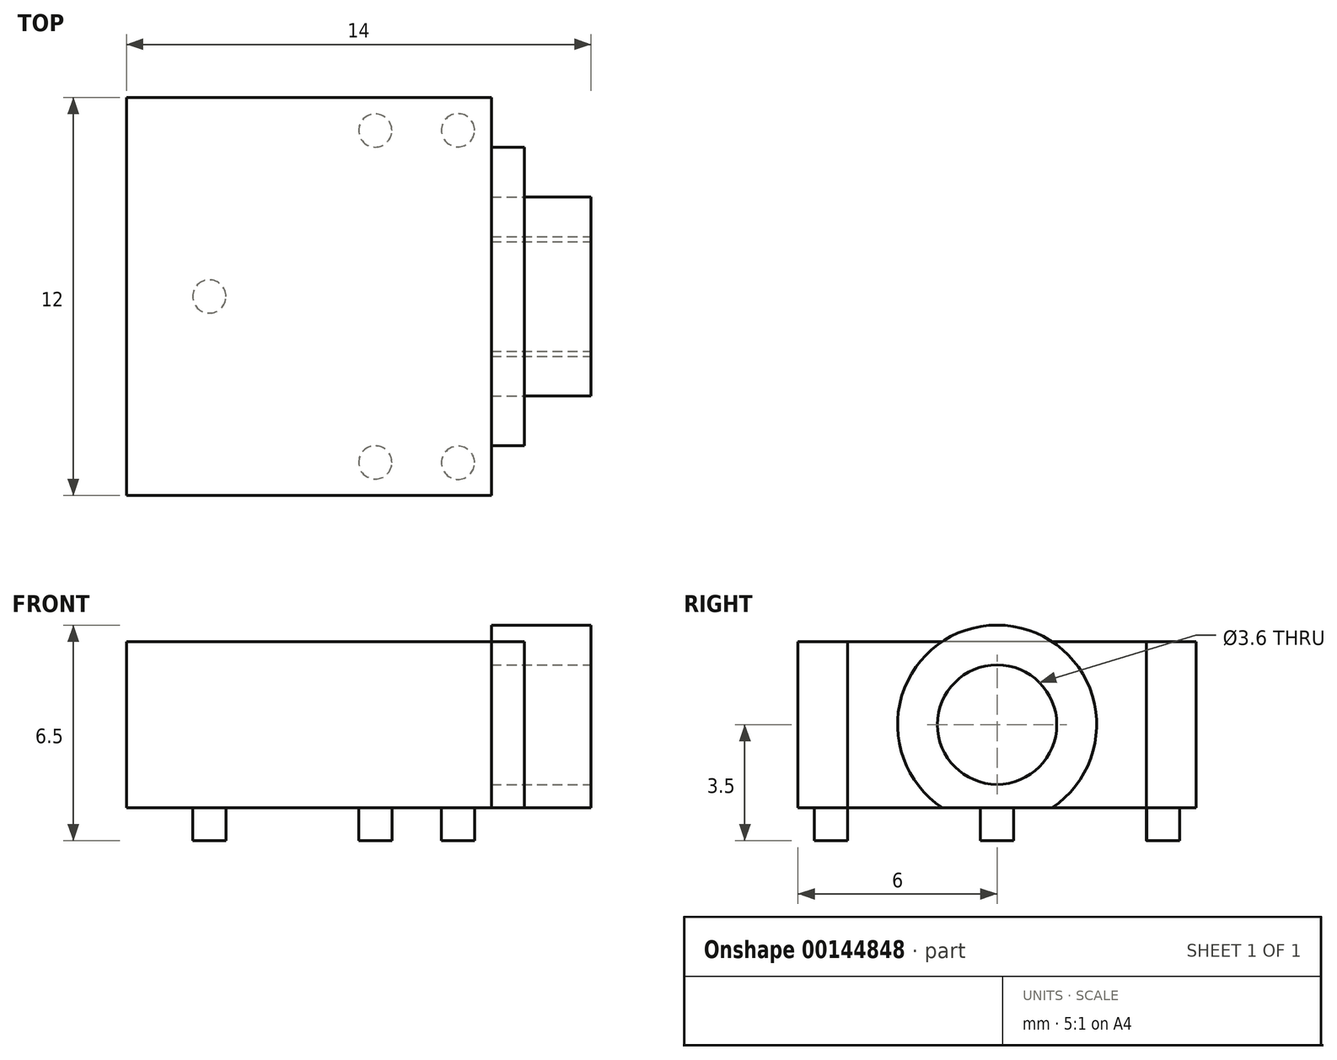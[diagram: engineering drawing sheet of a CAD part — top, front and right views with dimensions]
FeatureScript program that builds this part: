
annotation { "Feature Type Name" : "Feature", "Feature Type Description" : "" }
export const myFeature = defineFeature(function(context is Context, id is Id, definition is map)
    precondition{}
    {
        {
            var Q0;
            Q0=qCreatedBy(makeId("Right.planeOp"),FACE);
            var sketch = newSketch(context, id + "F0", { "sketchPlane" : qUnion([Q0])});
            skCircle(sketch, "E0", {"center": v(0, 0) * mm, "radius": 1.8 * mm});
            skCircle(sketch, "E1", {"center": v(0, 0) * mm, "radius": 3 * mm});
            skLineSegment(sketch, "E2.top", {"start": v(-1.65, -2.5) * mm, "end": v(4.5, -2.5) * mm});
            skLineSegment(sketch, "E3.top", {"start": v(4.5, -2.5) * mm, "end": v(6.02, -2.5) * mm});
            skSolve(sketch);
        }
        {
            var Q0;
            Q0=makeQuery(id+"F0.imprint","IMPRINT",FACE,{"disambiguationData":[TD([[makeQuery(id+"F0.imprint","IMPRINT",EDGE,{"derivedFrom":sQuery(id+"F0.wireOp",EDGE,"E0")}),-1.0]])]});
            var Q1;
            {var subQ0=sQuery(id+"F0.wireOp",EDGE,"E3.top");var subQ1=sQuery(id+"F0.wireOp",EDGE,"E1");var subQ2=makeQuery(id+"F0.imprint","INTERSECT",VERTEX,{"disambiguationData":[OD(0.0)],"derivedFrom":[subQ1,subQ0]});Q1=makeQuery(id+"F0.imprint","IMPRINT",FACE,{"disambiguationData":[TD([[makeQuery(id+"F0.imprint","IMPRINT",EDGE,{"disambiguationData":[TD([[subQ2,-1.0]])],"derivedFrom":subQ1}),1.0]])]});}
            var Q2;
            {var subQ0=sQuery(id+"F0.wireOp",EDGE,"E3.bottom");var subQ1=sQuery(id+"F0.wireOp",EDGE,"E1");var subQ2=makeQuery(id+"F0.imprint","INTERSECT",VERTEX,{"disambiguationData":[OD(0.0)],"derivedFrom":[subQ1,subQ0]});Q2=makeQuery(id+"F0.imprint","IMPRINT",FACE,{"disambiguationData":[TD([[makeQuery(id+"F0.imprint","IMPRINT",EDGE,{"disambiguationData":[TD([[subQ2,-1.0]])],"derivedFrom":subQ1}),1.0]])]});}
            extrude(context, id + "F1", {"entities" : qUnion([Q0, Q1, Q2]), "oppositeDirection" : true, "depth" : 3 * mm});
        }
        {
            var Q0;
            Q0=makeQuery(id+"F1.opExtrude","CAP_FACE",FACE,{"disambiguationData":[OSD([sQuery(id+"F0.wireOp",EDGE,"E0"),sQuery(id+"F0.wireOp",EDGE,"E1")])],"isStart":false});
            var sketch = newSketch(context, id + "F2", { "sketchPlane" : qUnion([Q0])});
            skLineSegment(sketch, "E4.bottom", {"start": v(-4.5, 2.5) * mm, "end": v(4.5, 2.5) * mm});
            skLineSegment(sketch, "E4.top", {"start": v(-4.5, -2.5) * mm, "end": v(4.5, -2.5) * mm});
            skLineSegment(sketch, "E4.left", {"start": v(-4.5, 2.5) * mm, "end": v(-4.5, -2.5) * mm});
            skLineSegment(sketch, "E4.right", {"start": v(4.5, 2.5) * mm, "end": v(4.5, -2.5) * mm});
            skSolve(sketch);
        }
        {
            var Q0;
            Q0 = qSketchRegion(id + "F2", true);
            extrude(context, id + "F3", {"entities" : qUnion([Q0]), "oppositeDirection" : true, "depth" : 1 * mm});
        }
        {
            var Q0;
            Q0=makeQuery(id+"F3.boolean.opBoolean","MERGE",FACE,{"derivedFrom":[makeQuery(id+"F1.opExtrude","CAP_FACE",FACE,{"disambiguationData":[OSD([sQuery(id+"F0.wireOp",EDGE,"E0"),sQuery(id+"F0.wireOp",EDGE,"E1")])],"isStart":false}),makeQuery(id+"F3.opExtrude","CAP_FACE",FACE,{"disambiguationData":[OSD([sQuery(id+"F2.wireOp",EDGE,"E4.bottom"),sQuery(id+"F2.wireOp",EDGE,"E4.top"),sQuery(id+"F2.wireOp",EDGE,"E4.left"),sQuery(id+"F2.wireOp",EDGE,"E4.right")])],"isStart":true})]});
            var sketch = newSketch(context, id + "F4", { "sketchPlane" : qUnion([Q0])});
            skLineSegment(sketch, "E5.bottom", {"start": v(-6, 2.5) * mm, "end": v(6, 2.5) * mm});
            skLineSegment(sketch, "E5.top", {"start": v(-6, -2.5) * mm, "end": v(6, -2.5) * mm});
            skLineSegment(sketch, "E5.left", {"start": v(-6, 2.5) * mm, "end": v(-6, -2.5) * mm});
            skLineSegment(sketch, "E5.right", {"start": v(6, 2.5) * mm, "end": v(6, -2.5) * mm});
            skSolve(sketch);
        }
        {
            var Q0;
            Q0 = qSketchRegion(id + "F4", true);
            extrude(context, id + "F5", {"entities" : qUnion([Q0]), "depth" : 11 * mm});
        }
        {
            var Q0;
            Q0=makeQuery(id+"F5.boolean.opBoolean","MERGE",FACE,{"derivedFrom":[dummyQuery(id+"FQrOcedIkoS32uB.importOp",FACE,7.0),makeQuery(id+"F5.opExtrude","SWEPT_FACE",FACE,{"disambiguationData":[OSD([sQuery(id+"F4.wireOp",EDGE,"E5.top")])]})]});
            var sketch = newSketch(context, id + "F6", { "sketchPlane" : qUnion([Q0])});
            skCircle(sketch, "E6", {"center": v(-6.5, 5) * mm, "radius": 0.5 * mm});
            skCircle(sketch, "E7", {"center": v(-4, -5) * mm, "radius": 0.5 * mm});
            skCircle(sketch, "E8", {"center": v(-6.5, -5) * mm, "radius": 0.5 * mm});
            skCircle(sketch, "E9", {"center": v(-11.5, 0) * mm, "radius": 0.5 * mm});
            skCircle(sketch, "E10", {"center": v(-4, 5) * mm, "radius": 0.5 * mm});
            skLineSegment(sketch, "E11", {"start": v(0, 0) * mm, "end": v(-14.57, 0) * mm, "construction": true});
            skSolve(sketch);
        }
        {
            var Q0;
            Q0=makeQuery(id+"F6.imprint","IMPRINT",FACE,{"disambiguationData":[TD([[makeQuery(id+"F6.imprint","IMPRINT",EDGE,{"derivedFrom":sQuery(id+"F6.wireOp",EDGE,"E10")}),1.0]])]});
            var Q1;
            Q1=makeQuery(id+"F6.imprint","IMPRINT",FACE,{"disambiguationData":[TD([[makeQuery(id+"F6.imprint","IMPRINT",EDGE,{"derivedFrom":sQuery(id+"F6.wireOp",EDGE,"E9")}),1.0]])]});
            var Q2;
            Q2=makeQuery(id+"F6.imprint","IMPRINT",FACE,{"disambiguationData":[TD([[makeQuery(id+"F6.imprint","IMPRINT",EDGE,{"derivedFrom":sQuery(id+"F6.wireOp",EDGE,"E8")}),1.0]])]});
            var Q3;
            Q3=makeQuery(id+"F6.imprint","IMPRINT",FACE,{"disambiguationData":[TD([[makeQuery(id+"F6.imprint","IMPRINT",EDGE,{"derivedFrom":sQuery(id+"F6.wireOp",EDGE,"E6")}),1.0]])]});
            var Q4;
            Q4=makeQuery(id+"F6.imprint","IMPRINT",FACE,{"disambiguationData":[TD([[makeQuery(id+"F6.imprint","IMPRINT",EDGE,{"derivedFrom":sQuery(id+"F6.wireOp",EDGE,"E7")}),1.0]])]});
            var Q5;
            Q5=sQuery(id+"F6.wireOp",EDGE,"E10");
            var Q6;
            Q6=sQuery(id+"F6.wireOp",EDGE,"E6");
            var Q7;
            Q7=sQuery(id+"F6.wireOp",EDGE,"E9");
            var Q8;
            Q8=sQuery(id+"F6.wireOp",EDGE,"E8");
            var Q9;
            Q9=sQuery(id+"F6.wireOp",EDGE,"E7");
            extrude(context, id + "F7", {"entities" : qUnion([Q0, Q1, Q2, Q3, Q4]), "surfaceEntities" : qUnion([Q5, Q6, Q7, Q8, Q9]), "depth" : 1 * mm});
        }
    });
